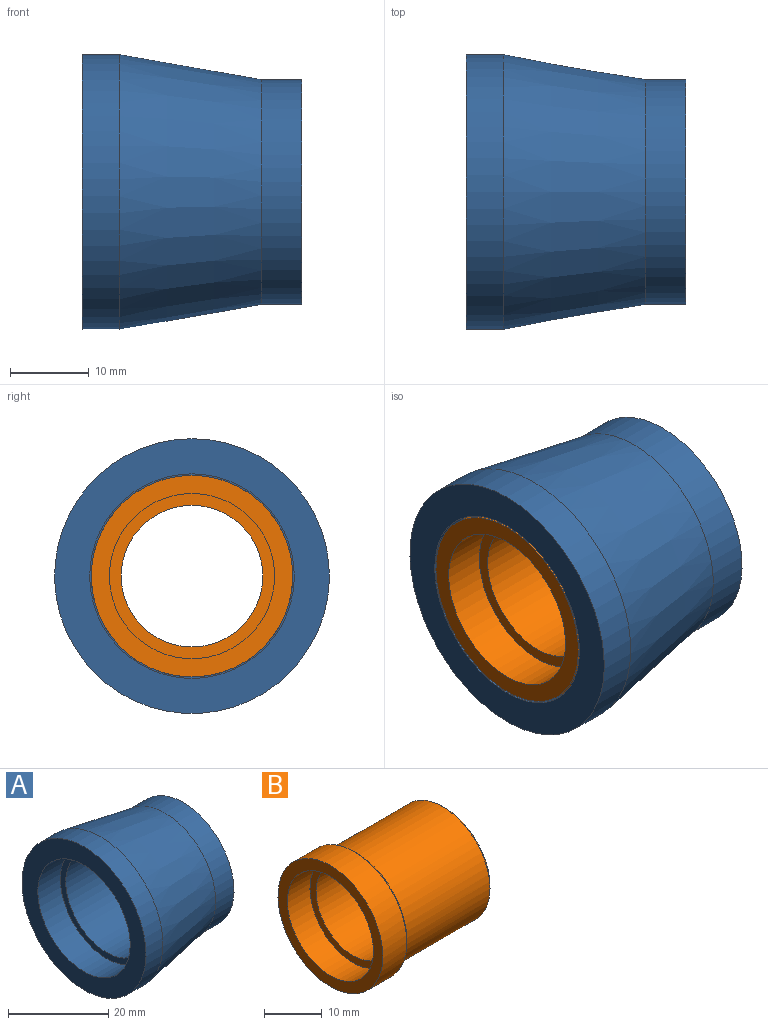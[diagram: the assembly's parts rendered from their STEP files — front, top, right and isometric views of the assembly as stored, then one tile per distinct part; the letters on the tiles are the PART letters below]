
ASSEMBLY  parts=2 mates=1
PART A: 8 faces, bbox 27.9x34.9x34.9 mm
  f0: cylinder r=17.46mm len=34.93mm, axis (-1,0,0), area 522.5mm2, adj f1,f7
  f1: plane 34.93x34.93mm, normal (-1,0,0), area 427.1mm2, adj f0,f2
  f2: cylinder r=13mm len=26mm, axis (-1,0,0), area 518.7mm2, adj f1,f3
  f3: plane 26x26mm, normal (-1,0,0), area 115.5mm2, adj f2,f4
  f4: cylinder r=11.5mm len=23mm, axis (-1,0,0), area 1560mm2, adj f3,f5
  f5: plane 28.58x28.58mm, normal (1,0,0), area 225.8mm2, adj f4,f6
  f6: cylinder r=14.29mm len=28.58mm, axis (-1,0,0), area 464.2mm2, adj f5,f7
  f7: cone r=17.46mm half-angle=10deg, axis (-1,0,0), area 1823.8mm2, adj f0,f6
PART B: 12 faces, bbox 27.9x25.6x25.6 mm
  f0: cylinder r=12.8mm len=25.6mm, axis (-1,0,0), area 469.8mm2, adj f1,f6
  f1: plane 25.6x25.6mm, normal (-1,0,0), area 168.4mm2, adj f0,f10
  f2: plane 22.02x22.02mm, normal (1,0,0), area 34.6mm2, adj f5,f7
  f3: cylinder r=11.52mm len=23.04mm, axis (-1,0,0), area 1526mm2, adj f4,f5
  f4: plane 24.58x24.58mm, normal (1,0,0), area 57.8mm2, adj f3,f6
  f5: cone r=11.52mm half-angle=45deg, axis (-1,0,0), area 50.9mm2, adj f2,f3
  f6: cone r=12.8mm half-angle=45deg, axis (-1,0,0), area 56.6mm2, adj f0,f4
  f7: cylinder r=10.5mm len=21mm, axis (-1,0,0), area 362.9mm2, adj f2,f8
  f8: plane 21x21mm, normal (1,0,0), area 91.9mm2, adj f7,f9
  f9: cylinder r=9mm len=18mm, axis (-1,0,0), area 957.9mm2, adj f8,f11
  f10: cylinder r=10.5mm len=21mm, axis (-1,0,0), area 362.9mm2, adj f1,f11
  f11: plane 21x21mm, normal (-1,0,0), area 91.9mm2, adj f9,f10
PLACE A t=(2.24,8.58,0.47)mm fixed
PLACE B t=(2.24,8.58,0.47)mm
MATE fastened B.f0 <-> A.f0  axis (1,0,0) through (8.59,8.58,0.47)mm
